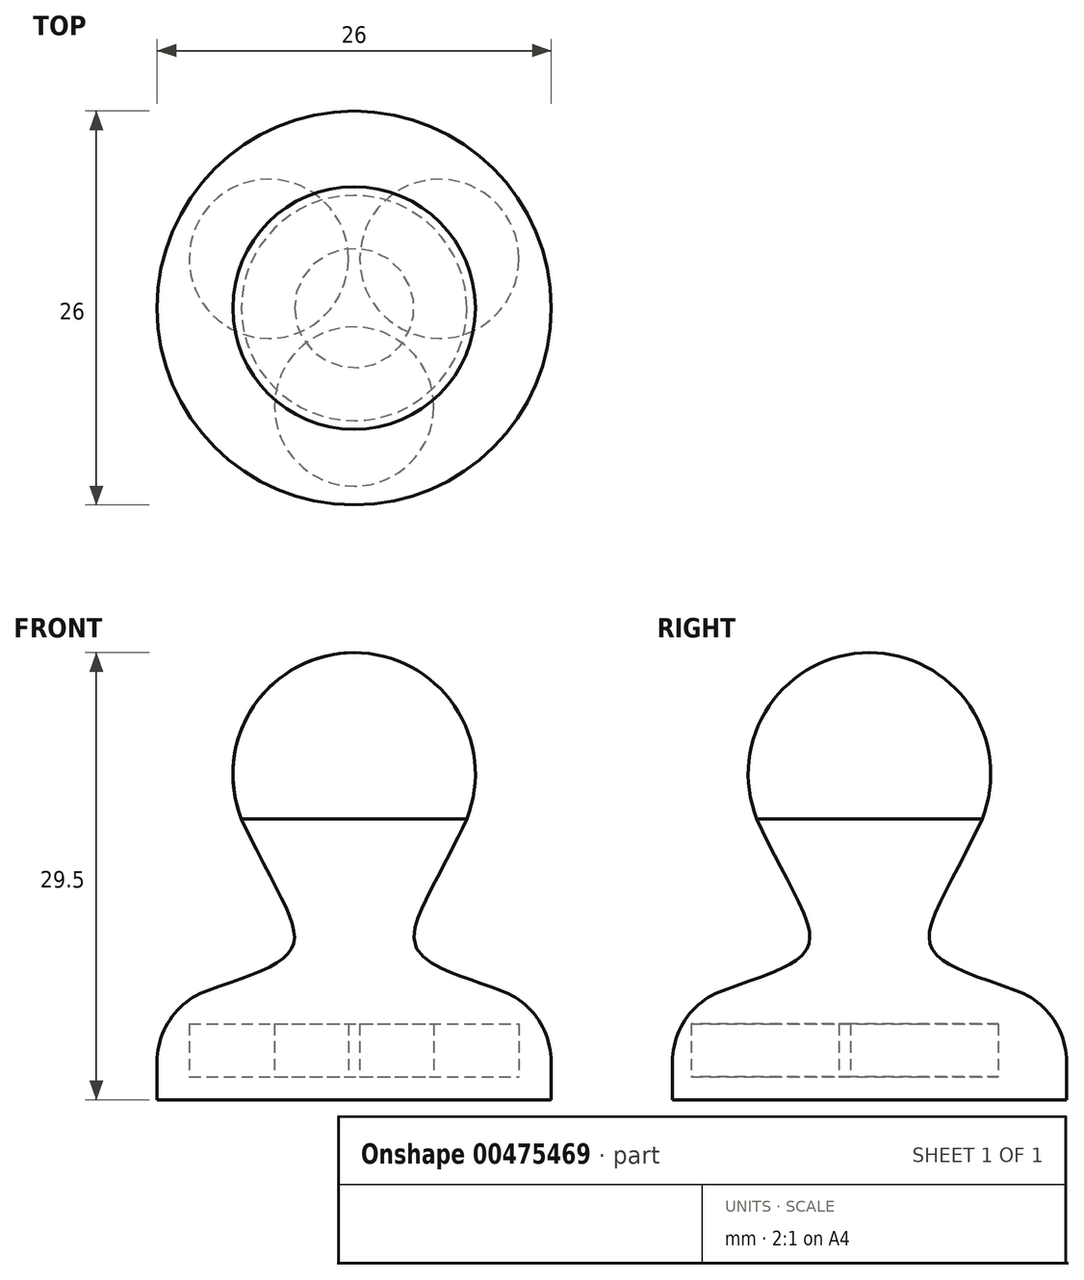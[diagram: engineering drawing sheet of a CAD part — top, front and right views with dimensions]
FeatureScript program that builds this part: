
annotation { "Feature Type Name" : "Feature", "Feature Type Description" : "" }
export const myFeature = defineFeature(function(context is Context, id is Id, definition is map)
    precondition{}
    {
        {
            var Q0;
            Q0=qCreatedBy(makeId("Front.planeOp"),FACE);
            var sketch = newSketch(context, id + "F0", { "sketchPlane" : qUnion([Q0])});
            skLineSegment(sketch, "E0", {"start": v(0, 0) * mm, "end": v(-13, 0) * mm});
            skLineSegment(sketch, "E1", {"start": v(-13, 0) * mm, "end": v(-13, 1) * mm});
            skArc(sketch, "E2", {"start": v(0, 28) * mm, "mid": v(-6.62, 24.5) * mm, "end": v(-7.43, 17.04) * mm});
            skFitSpline(sketch, "E3", {"points": [v(-7.43, 17.04) * mm, v(-4.22, 8.3) * mm, v(-13, 4.35) * mm], "startDerivative": vector(13.82, -30.03) * mm, "endDerivative": vector(-21.35, -10.48) * mm});
            skArc(sketch, "E4.filletArc", {"start": v(-9.68, 5.7) * mm, "mid": v(-12.09, 3.88) * mm, "end": v(-13, 1) * mm});
            skLineSegment(sketch, "E5", {"start": v(0, 0) * mm, "end": v(0, 28) * mm});
            skSolve(sketch);
        }
        {
            var Q0;
            Q0=makeQuery(id+"F0.imprint","IMPRINT",FACE,{"disambiguationData":[TD([[makeQuery(id+"F0.imprint","IMPRINT",EDGE,{"derivedFrom":sQuery(id+"F0.wireOp",EDGE,"E0")}),-1.0]])]});
            var Q1;
            Q1=sQuery(id+"F0.wireOp",EDGE,"E3");
            var Q2;
            Q2=sQuery(id+"F0.wireOp",EDGE,"E5");
            revolve(context, id + "F1", {"entities" : qUnion([Q0]), "surfaceEntities" : qUnion([Q1]), "axis" : qUnion([Q2]), "revolveType" : RevolveType.FULL});
        }
        {
            var Q0;
            Q0=makeQuery(id+"F1.opRevolve","SWEPT_FACE",FACE,{"disambiguationData":[OSD([sQuery(id+"F0.wireOp",EDGE,"E0")])]});
            var sketch = newSketch(context, id + "F2", { "sketchPlane" : qUnion([Q0])});
            skCircle(sketch, "E6", {"center": v(0, 6.5) * mm, "radius": 5.25 * mm});
            skCircle(sketch, "E7.1.0", {"center": v(-5.63, -3.25) * mm, "radius": 5.25 * mm});
            skCircle(sketch, "E7.2.0", {"center": v(5.63, -3.25) * mm, "radius": 5.25 * mm});
            skPoint(sketch, "E7.center", {"position": v(0, 0) * mm});
            skSolve(sketch);
        }
        {
            var Q0;
            Q0=makeQuery(id+"F2.imprint","IMPRINT",FACE,{"disambiguationData":[TD([[makeQuery(id+"F2.imprint","IMPRINT",EDGE,{"derivedFrom":sQuery(id+"F2.wireOp",EDGE,"E7.1.0")}),1.0]])]});
            var Q1;
            Q1=makeQuery(id+"F2.imprint","IMPRINT",FACE,{"disambiguationData":[TD([[makeQuery(id+"F2.imprint","IMPRINT",EDGE,{"derivedFrom":sQuery(id+"F2.wireOp",EDGE,"E7.2.0")}),1.0]])]});
            var Q2;
            Q2=makeQuery(id+"F2.imprint","IMPRINT",FACE,{"disambiguationData":[TD([[makeQuery(id+"F2.imprint","IMPRINT",EDGE,{"derivedFrom":sQuery(id+"F2.wireOp",EDGE,"E6")}),1.0]])]});
            extrude(context, id + "F3", {"entities" : qUnion([Q0, Q1, Q2]), "operationType" : NewBodyOperationType.REMOVE, "oppositeDirection" : true, "depth" : 3.5 * mm});
        }
        {
            var Q0;
            Q0=makeQuery(id+"F1.opRevolve","SWEPT_FACE",FACE,{"disambiguationData":[OSD([sQuery(id+"F0.wireOp",EDGE,"E0")])]});
            var sketch = newSketch(context, id + "F4", { "sketchPlane" : qUnion([Q0])});
            skCircle(sketch, "E8.0", {"center": v(0, 0) * mm, "radius": 13 * mm});
            skSolve(sketch);
        }
        {
            var Q0;
            Q0 = qSketchRegion(id + "F4", true);
            extrude(context, id + "F5", {"entities" : qUnion([Q0]), "operationType" : NewBodyOperationType.ADD, "depth" : 1.5 * mm});
        }
    });
